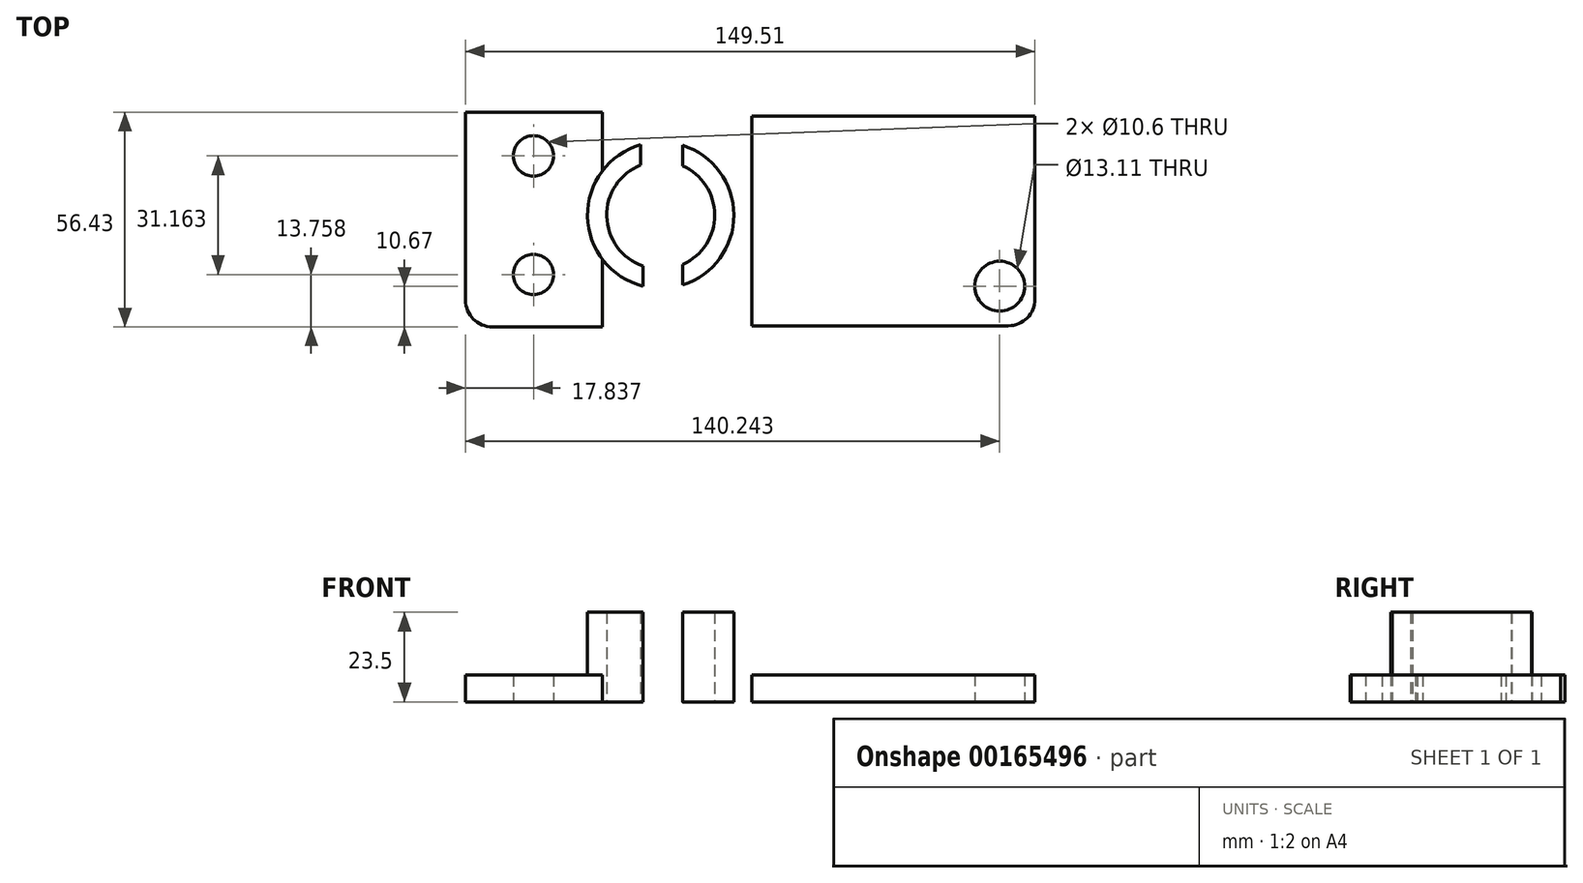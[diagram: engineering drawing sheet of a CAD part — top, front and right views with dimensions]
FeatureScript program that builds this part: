
annotation { "Feature Type Name" : "Feature", "Feature Type Description" : "" }
export const myFeature = defineFeature(function(context is Context, id is Id, definition is map)
    precondition{}
    {
        {
            var Q0;
            Q0=qCreatedBy(makeId("Top.planeOp"),FACE);
            var sketch = newSketch(context, id + "F0", { "sketchPlane" : qUnion([Q0])});
            skLineSegment(sketch, "E0.bottom", {"start": v(-75.22, 27.1) * mm, "end": v(-39.28, 27.1) * mm});
            skLineSegment(sketch, "E0.top", {"start": v(-75.22, -29.34) * mm, "end": v(-39.28, -29.34) * mm});
            skLineSegment(sketch, "E0.left", {"start": v(-75.22, 27.1) * mm, "end": v(-75.22, -29.34) * mm});
            skLineSegment(sketch, "E0.right", {"start": v(-39.28, 27.1) * mm, "end": v(-39.28, -29.34) * mm});
            skCircle(sketch, "E1", {"center": v(-57.38, 15.58) * mm, "radius": 5.3 * mm});
            skCircle(sketch, "E2.MirrorC", {"center": v(-57.38, -15.58) * mm, "radius": 5.3 * mm});
            skSolve(sketch);
        }
        {
            var Q0;
            Q0 = qSketchRegion(id + "F0", true);
            extrude(context, id + "F1", {"entities" : qUnion([Q0]), "depth" : 7 * mm});
        }
        {
            var Q0;
            Q0=makeQuery(id+"F1.opExtrude","SWEPT_EDGE",EDGE,{"disambiguationData":[OSD([sQuery(id+"F0.wireOp",EDGE,"E0.top"),sQuery(id+"F0.wireOp",EDGE,"E0.left")])]});
            fillet(context, id + "F2", {"entities" : qUnion([Q0]), "radius" : 7 * mm, "tangentPropagation" : true, "allowEdgeOverflow" : false});
        }
        {
            var Q0;
            Q0=qCreatedBy(makeId("Top.planeOp"),FACE);
            var sketch = newSketch(context, id + "F3", { "sketchPlane" : qUnion([Q0])});
            skCircle(sketch, "E3", {"center": v(-23.97, 0) * mm, "radius": 19.21 * mm});
            skCircle(sketch, "E4", {"center": v(-23.97, 0) * mm, "radius": 14.18 * mm});
            skLineSegment(sketch, "E5", {"start": v(-29.24, 13.16) * mm, "end": v(-29.24, 18.48) * mm});
            skLineSegment(sketch, "E6", {"start": v(-18.27, 12.98) * mm, "end": v(-18.27, 18.35) * mm});
            skLineSegment(sketch, "E7", {"start": v(-28.66, -13.38) * mm, "end": v(-28.66, -18.63) * mm});
            skLineSegment(sketch, "E8", {"start": v(-18.15, -12.93) * mm, "end": v(-18.15, -18.3) * mm});
            skSolve(sketch);
        }
        {
            var Q0;
            {var subQ0=sQuery(id+"F3.wireOp",EDGE,"E5");Q0=makeQuery(id+"F3.imprint","IMPRINT",FACE,{"disambiguationData":[TD([[makeQuery(id+"F3.imprint","IMPRINT",EDGE,{"derivedFrom":subQ0}),1.0]])]});}
            var Q1;
            {var subQ0=sQuery(id+"F3.wireOp",EDGE,"E6");Q1=makeQuery(id+"F3.imprint","IMPRINT",FACE,{"disambiguationData":[TD([[makeQuery(id+"F3.imprint","IMPRINT",EDGE,{"derivedFrom":subQ0}),-1.0]])]});}
            extrude(context, id + "F4", {"entities" : qUnion([Q0, Q1]), "operationType" : NewBodyOperationType.ADD, "depth" : 23.5 * mm});
        }
        {
            var Q0;
            Q0=qCreatedBy(makeId("Top.planeOp"),FACE);
            var sketch = newSketch(context, id + "F5", { "sketchPlane" : qUnion([Q0])});
            skLineSegment(sketch, "E9.bottom", {"start": v(0, -29.06) * mm, "end": v(74.29, -29.06) * mm});
            skLineSegment(sketch, "E9.top", {"start": v(0, 25.97) * mm, "end": v(74.29, 25.97) * mm});
            skLineSegment(sketch, "E9.left", {"start": v(0, -29.06) * mm, "end": v(0, 25.97) * mm});
            skLineSegment(sketch, "E9.right", {"start": v(74.29, -29.06) * mm, "end": v(74.29, 25.97) * mm});
            skCircle(sketch, "E10", {"center": v(65.02, -18.67) * mm, "radius": 6.55 * mm});
            skSolve(sketch);
        }
        {
            var Q0;
            Q0 = qSketchRegion(id + "F5", true);
            extrude(context, id + "F6", {"entities" : qUnion([Q0]), "depth" : 7.1 * mm});
        }
        {
            var Q0;
            Q0=makeQuery(id+"F6.opExtrude","SWEPT_EDGE",EDGE,{"disambiguationData":[OSD([sQuery(id+"F5.wireOp",EDGE,"E9.bottom"),sQuery(id+"F5.wireOp",EDGE,"E9.right")])]});
            fillet(context, id + "F7", {"entities" : qUnion([Q0]), "radius" : 7 * mm, "tangentPropagation" : true, "allowEdgeOverflow" : false});
        }
    });
